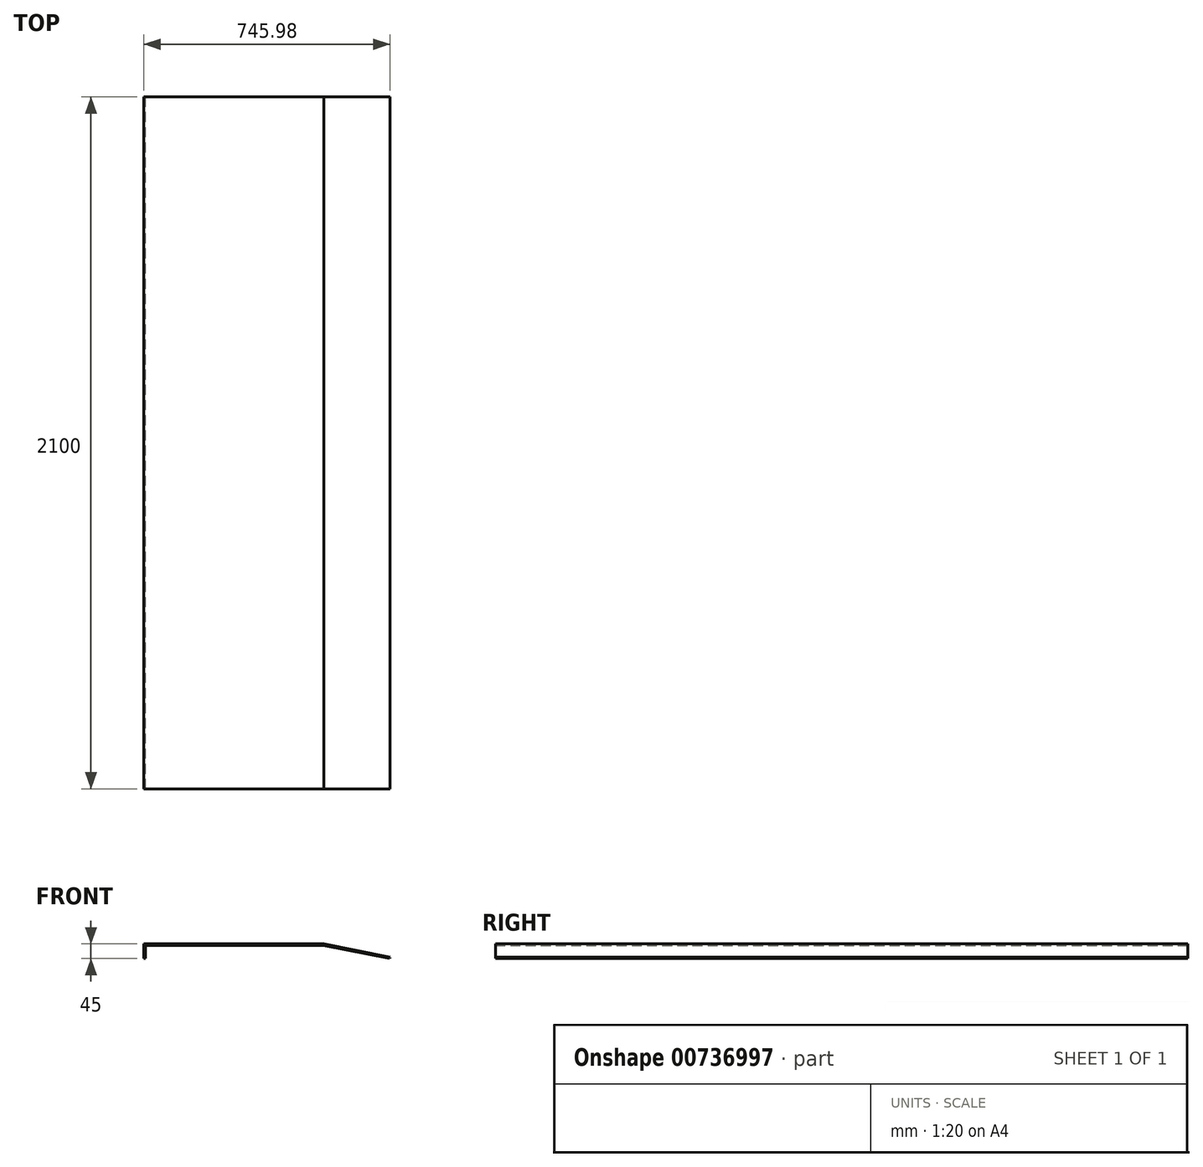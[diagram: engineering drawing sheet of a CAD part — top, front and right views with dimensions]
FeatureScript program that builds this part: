
annotation { "Feature Type Name" : "Feature", "Feature Type Description" : "" }
export const myFeature = defineFeature(function(context is Context, id is Id, definition is map)
    precondition{}
    {
        {
            var Q0;
            Q0=qCreatedBy(makeId("Front.planeOp"),FACE);
            var sketch = newSketch(context, id + "F0", { "sketchPlane" : qUnion([Q0])});
            skLineSegment(sketch, "E0", {"start": v(0, 0) * mm, "end": v(0, 40) * mm});
            skLineSegment(sketch, "E1", {"start": v(0, 40) * mm, "end": v(540, 40) * mm});
            skLineSegment(sketch, "E2", {"start": v(540, 40) * mm, "end": v(740, 0) * mm});
            skLineSegment(sketch, "E3", {"start": v(540, 40) * mm, "end": v(540, 0) * mm});
            skLineSegment(sketch, "E4", {"start": v(540, 0) * mm, "end": v(740, 0) * mm});
            skLineSegment(sketch, "E5.0", {"start": v(540.5, 45) * mm, "end": v(740.98, 4.9) * mm});
            skLineSegment(sketch, "E5.1", {"start": v(-5, 45) * mm, "end": v(540.5, 45) * mm});
            skLineSegment(sketch, "E5.2", {"start": v(-5, 0) * mm, "end": v(-5, 45) * mm});
            skLineSegment(sketch, "E6", {"start": v(-5, 0) * mm, "end": v(0, 0) * mm});
            skLineSegment(sketch, "E7", {"start": v(740.98, 4.9) * mm, "end": v(740, 0) * mm});
            skSolve(sketch);
        }
        {
            var Q0;
            Q0=makeQuery(id+"F0.imprint","IMPRINT",FACE,{"disambiguationData":[TD([[makeQuery(id+"F0.imprint","IMPRINT",EDGE,{"derivedFrom":sQuery(id+"F0.wireOp",EDGE,"E0")}),1.0]])]});
            extrude(context, id + "F1", {"entities" : qUnion([Q0]), "depth" : 2100 * mm, "offsetDistance" : 25 * mm});
        }
    });
